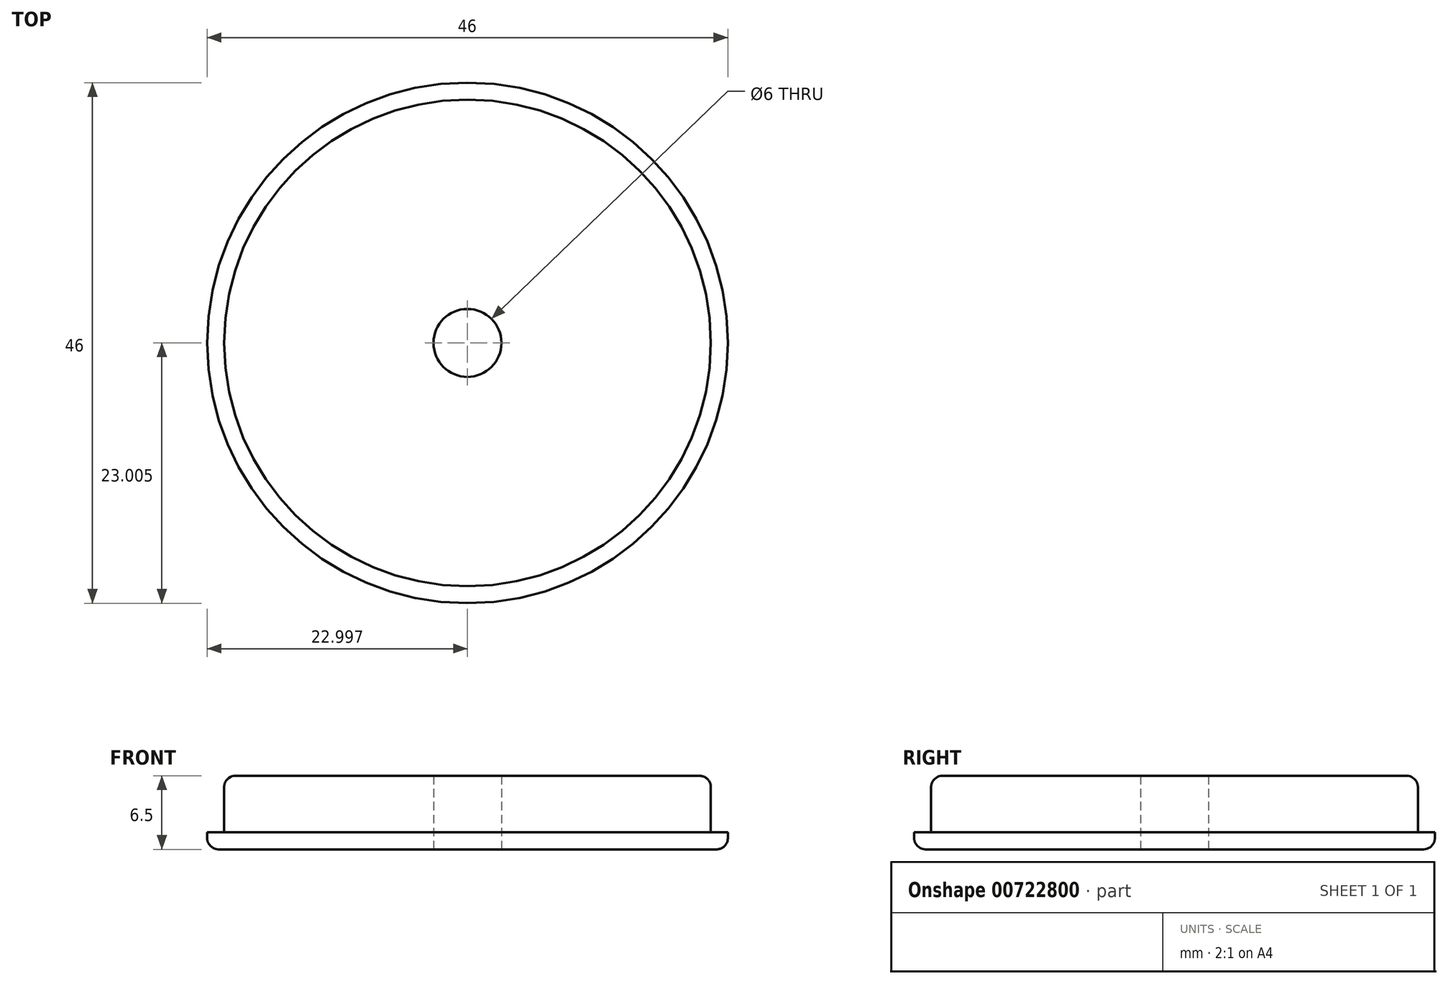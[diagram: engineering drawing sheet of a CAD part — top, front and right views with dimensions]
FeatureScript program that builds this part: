
annotation { "Feature Type Name" : "Feature", "Feature Type Description" : "" }
export const myFeature = defineFeature(function(context is Context, id is Id, definition is map)
    precondition{}
    {
        {
            var Q0;
            Q0=qCreatedBy(makeId("Top.planeOp"),FACE);
            var sketch = newSketch(context, id + "F0", { "sketchPlane" : qUnion([Q0])});
            skCircle(sketch, "E0", {"center": v(9.7, 15.35) * mm, "radius": 23 * mm});
            skCircle(sketch, "E1", {"center": v(9.7, 15.35) * mm, "radius": 3 * mm});
            skCircle(sketch, "E2", {"center": v(9.7, 15.35) * mm, "radius": 21.5 * mm});
            skSolve(sketch);
        }
        {
            var Q0;
            Q0 = qSketchRegion(id + "F0", true);
            extrude(context, id + "F1", {"entities" : qUnion([Q0]), "depth" : 1.5 * mm, "offsetDistance" : 25 * mm});
        }
        {
            var Q0;
            Q0=makeQuery(id+"F0.imprint","IMPRINT",FACE,{"disambiguationData":[TD([[makeQuery(id+"F0.imprint","IMPRINT",EDGE,{"derivedFrom":sQuery(id+"F0.wireOp",EDGE,"E1")}),-1.0]])]});
            extrude(context, id + "F2", {"entities" : qUnion([Q0]), "operationType" : NewBodyOperationType.ADD, "depth" : 6.5 * mm, "offsetDistance" : 25 * mm});
        }
        {
            var Q0;
            Q0=makeQuery(id+"F2.opExtrude","CAP_EDGE",EDGE,{"disambiguationData":[OSD([sQuery(id+"F0.wireOp",EDGE,"E2")])],"isStart":false});
            fillet(context, id + "F3", {"entities" : qUnion([Q0]), "radius" : 1 * mm, "tangentPropagation" : true, "allowEdgeOverflow" : false});
        }
        {
            var Q0;
            Q0=makeQuery(id+"F1.opExtrude","CAP_EDGE",EDGE,{"disambiguationData":[OSD([sQuery(id+"F0.wireOp",EDGE,"E0")])],"isStart":true});
            fillet(context, id + "F4", {"entities" : qUnion([Q0]), "radius" : 1 * mm, "tangentPropagation" : true, "allowEdgeOverflow" : false});
        }
    });
